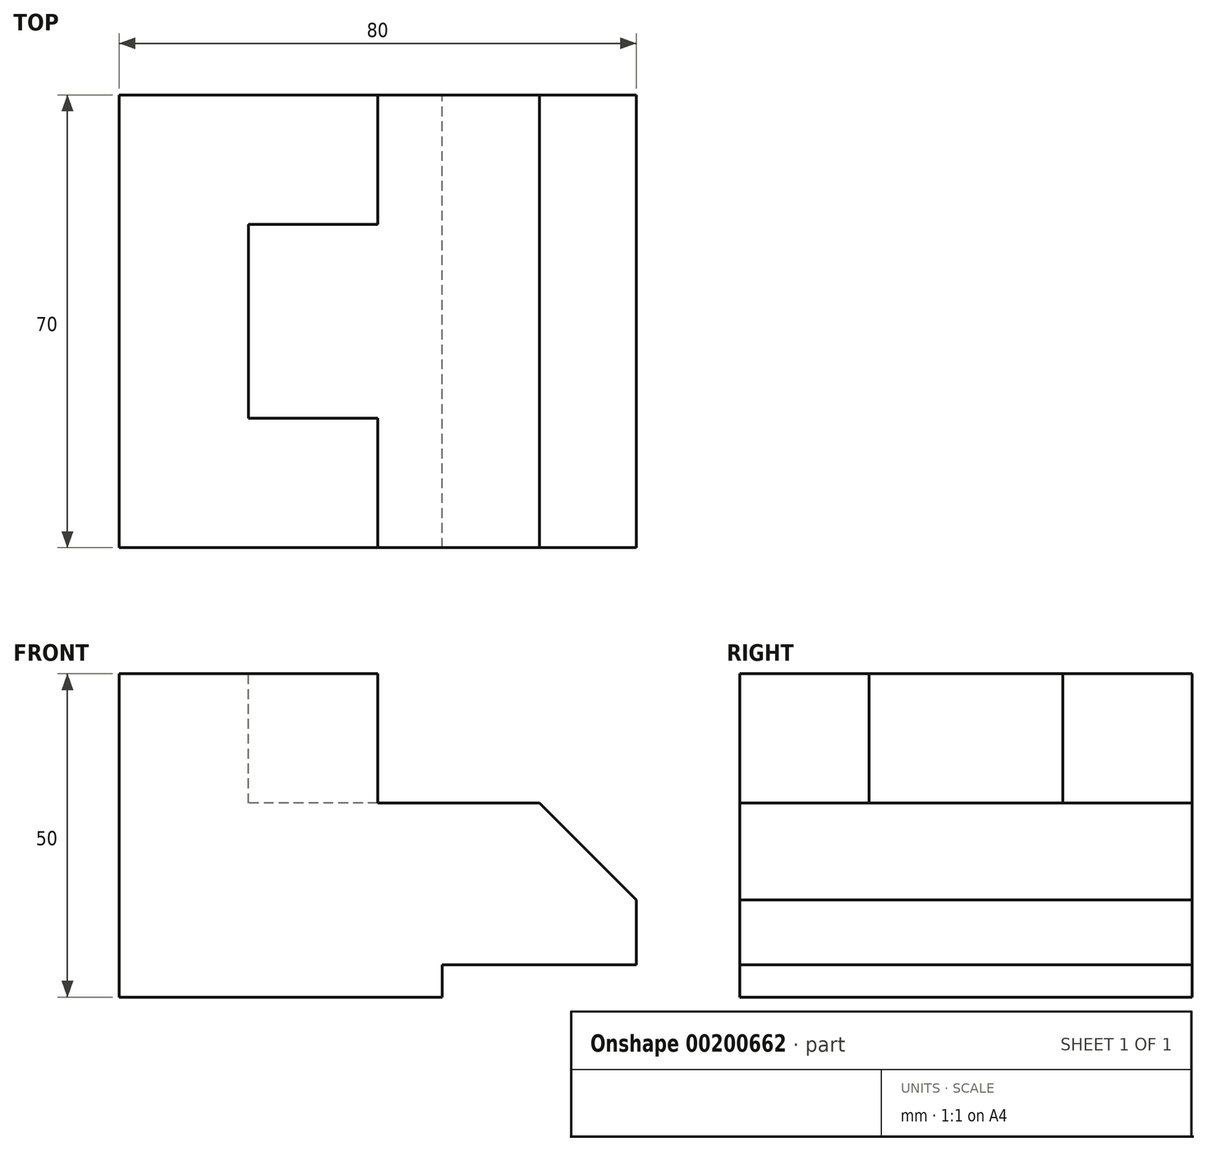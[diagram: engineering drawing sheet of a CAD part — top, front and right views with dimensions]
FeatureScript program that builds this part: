
annotation { "Feature Type Name" : "Feature", "Feature Type Description" : "" }
export const myFeature = defineFeature(function(context is Context, id is Id, definition is map)
    precondition{}
    {
        {
            var Q0;
            Q0=qCreatedBy(makeId("Front.planeOp"),FACE);
            var sketch = newSketch(context, id + "F0", { "sketchPlane" : qUnion([Q0])});
            skLineSegment(sketch, "E0", {"start": v(-50, 0) * mm, "end": v(0, 0) * mm});
            skLineSegment(sketch, "E1", {"start": v(0, 0) * mm, "end": v(0, 5) * mm});
            skLineSegment(sketch, "E2", {"start": v(0, 5) * mm, "end": v(30, 5) * mm});
            skLineSegment(sketch, "E3", {"start": v(30, 5) * mm, "end": v(30, 15) * mm});
            skLineSegment(sketch, "E4", {"start": v(30, 15) * mm, "end": v(15, 30) * mm});
            skLineSegment(sketch, "E5", {"start": v(15, 30) * mm, "end": v(-10, 30) * mm});
            skLineSegment(sketch, "E6", {"start": v(-10, 30) * mm, "end": v(-10, 50) * mm});
            skLineSegment(sketch, "E7", {"start": v(-10, 50) * mm, "end": v(-50, 50) * mm});
            skLineSegment(sketch, "E8", {"start": v(-50, 50) * mm, "end": v(-50, 0) * mm});
            skSolve(sketch);
        }
        {
            var Q0;
            Q0=makeQuery(id+"F0.imprint","IMPRINT",FACE,{"disambiguationData":[TD([[makeQuery(id+"F0.imprint","IMPRINT",EDGE,{"derivedFrom":sQuery(id+"F0.wireOp",EDGE,"E0")}),1.0]])]});
            extrude(context, id + "F1", {"entities" : qUnion([Q0]), "depth" : 70 * mm});
        }
        {
            var Q0;
            Q0=makeQuery(id+"F1.opExtrude","SWEPT_FACE",FACE,{"disambiguationData":[OSD([sQuery(id+"F0.wireOp",EDGE,"E7")])]});
            var sketch = newSketch(context, id + "F2", { "sketchPlane" : qUnion([Q0])});
            skLineSegment(sketch, "E9.0.0", {"start": v(-10, 0) * mm, "end": v(-50, 0) * mm});
            skLineSegment(sketch, "E9.0.1", {"start": v(-50, 0) * mm, "end": v(-50, -70) * mm});
            skLineSegment(sketch, "E9.0.2", {"start": v(-50, -70) * mm, "end": v(-10, -70) * mm});
            skLineSegment(sketch, "E9.0.3", {"start": v(-10, -70) * mm, "end": v(-10, 0) * mm});
            skLineSegment(sketch, "E10", {"start": v(-10, -20) * mm, "end": v(-30, -20) * mm});
            skLineSegment(sketch, "E11", {"start": v(-30, -20) * mm, "end": v(-30, -50) * mm});
            skLineSegment(sketch, "E12", {"start": v(-30, -50) * mm, "end": v(-10, -50) * mm});
            skSolve(sketch);
        }
        {
            var Q0;
            {var subQ0=sQuery(id+"F2.wireOp",EDGE,"E10");Q0=makeQuery(id+"F2.imprint","IMPRINT",FACE,{"disambiguationData":[TD([[makeQuery(id+"F2.imprint","IMPRINT",EDGE,{"derivedFrom":subQ0}),1.0]])]});}
            extrude(context, id + "F3", {"entities" : qUnion([Q0]), "operationType" : NewBodyOperationType.REMOVE, "oppositeDirection" : true, "depth" : 20 * mm});
        }
    });
